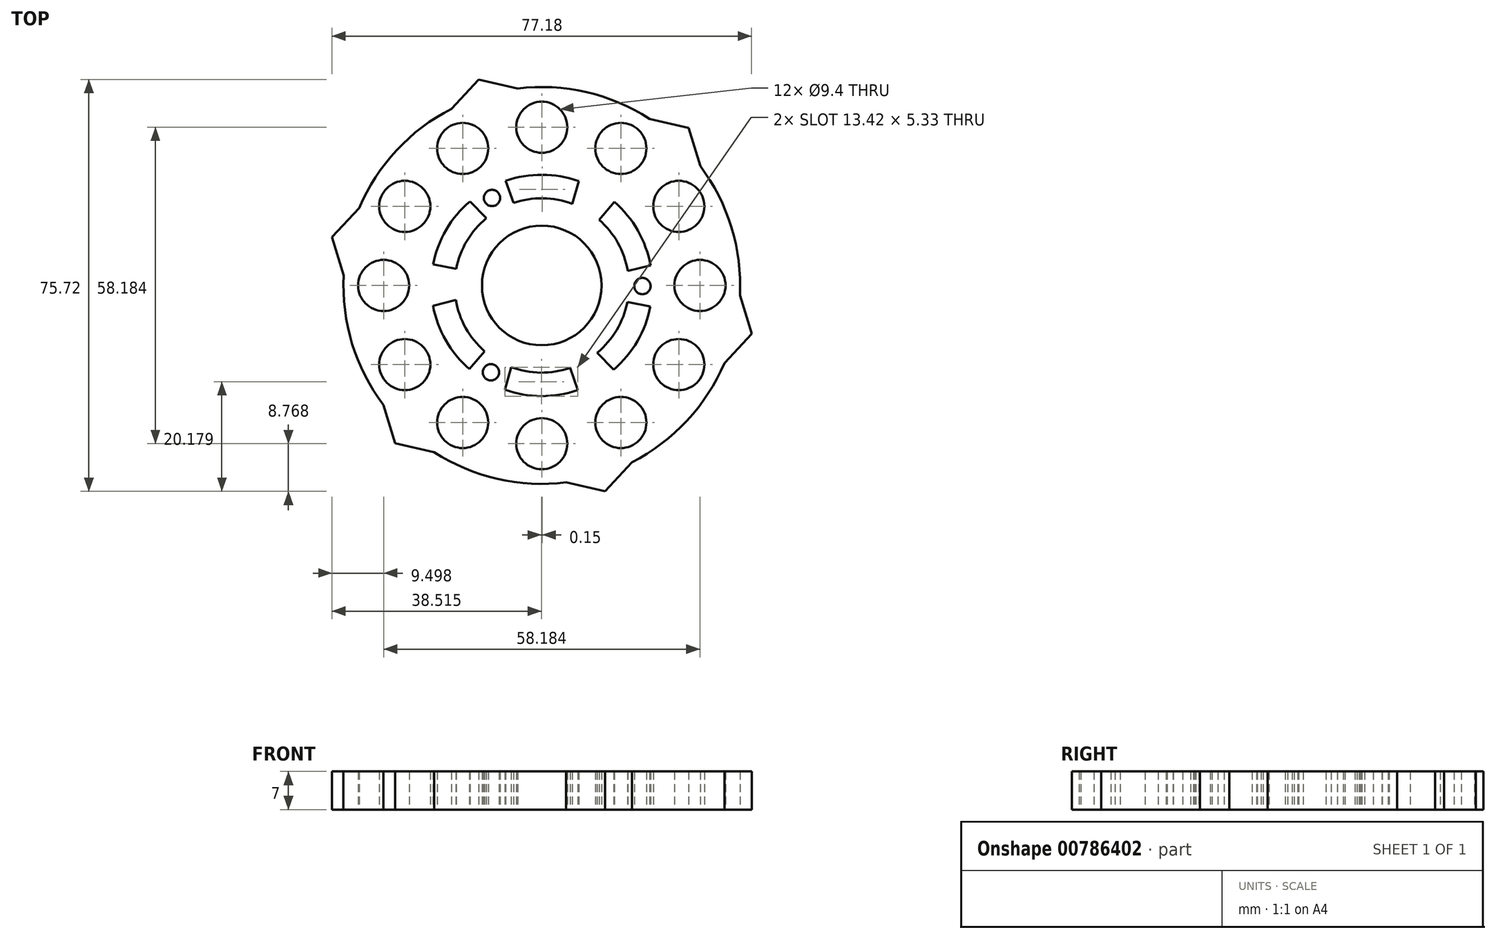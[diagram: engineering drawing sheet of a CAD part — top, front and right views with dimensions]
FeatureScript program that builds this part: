
annotation { "Feature Type Name" : "Feature", "Feature Type Description" : "" }
export const myFeature = defineFeature(function(context is Context, id is Id, definition is map)
    precondition{}
    {
        {
            var Q0;
            Q0=qCreatedBy(makeId("Top.planeOp"),FACE);
            var sketch = newSketch(context, id + "F0", { "sketchPlane" : qUnion([Q0])});
            skArc(sketch, "E0", {"start": v(-9.53, -5.5) * mm, "mid": v(0, -11) * mm, "end": v(9.53, -5.5) * mm});
            skArc(sketch, "E1", {"start": v(-19.81, -30.63) * mm, "mid": v(-8.17, -35.55) * mm, "end": v(4.44, -36.2) * mm});
            skLineSegment(sketch, "E2.2", {"start": v(11.61, -37.86) * mm, "end": v(4.44, -36.2) * mm});
            skLineSegment(sketch, "E2.3", {"start": v(-26.98, -28.98) * mm, "end": v(-29.14, -21.95) * mm});
            skLineSegment(sketch, "E2.5", {"start": v(-11.61, 37.86) * mm, "end": v(-4.44, 36.2) * mm});
            skArc(sketch, "E3.trimOffspring", {"start": v(16.62, -32.47) * mm, "mid": v(25.14, -26.44) * mm, "end": v(31.6, -18.24) * mm});
            skLineSegment(sketch, "E4.trimOffspring", {"start": v(-19.81, -30.63) * mm, "end": v(-26.98, -28.98) * mm});
            skLineSegment(sketch, "E5.trimOffspring", {"start": v(16.62, -32.47) * mm, "end": v(11.61, -37.86) * mm});
            skLineSegment(sketch, "E6.trimOffspring", {"start": v(-16.62, 32.47) * mm, "end": v(-11.61, 37.86) * mm});
            skArc(sketch, "E7.trimOffspring", {"start": v(-31.6, -18.24) * mm, "mid": v(-30.42, -20.13) * mm, "end": v(-29.14, -21.95) * mm});
            skPoint(sketch, "E8.trimOffspring.end.orphan", {"position": v(42.43, -24.5) * mm});
            skPoint(sketch, "E9.MirrorCS.end.orphan", {"position": v(-42.43, -24.5) * mm});
            skArc(sketch, "E10.1.0", {"start": v(19.81, 30.63) * mm, "mid": v(10.33, 34.99) * mm, "end": v(0, 36.48) * mm});
            skLineSegment(sketch, "E10.1.6", {"start": v(38.6, -8.87) * mm, "end": v(33.58, -14.26) * mm});
            skLineSegment(sketch, "E10.1.7", {"start": v(36.43, -1.84) * mm, "end": v(38.6, -8.87) * mm});
            skArc(sketch, "E10.1.8", {"start": v(31.6, -18.24) * mm, "mid": v(32.65, -16.28) * mm, "end": v(33.58, -14.26) * mm});
            skArc(sketch, "E10.1.9", {"start": v(36.43, -1.84) * mm, "mid": v(34.88, 10.7) * mm, "end": v(29.14, 21.95) * mm});
            skLineSegment(sketch, "E10.1.10", {"start": v(26.98, 28.98) * mm, "end": v(29.14, 21.95) * mm});
            skArc(sketch, "E10.1.11", {"start": v(9.53, -5.5) * mm, "mid": v(9.53, 5.5) * mm, "end": v(0, 11) * mm});
            skLineSegment(sketch, "E10.1.12", {"start": v(19.81, 30.63) * mm, "end": v(26.98, 28.98) * mm});
            skArc(sketch, "E10.2.0", {"start": v(-36.43, 1.84) * mm, "mid": v(-35.46, -8.55) * mm, "end": v(-31.6, -18.24) * mm});
            skArc(sketch, "E10.2.8", {"start": v(0, 36.48) * mm, "mid": v(-2.23, 36.41) * mm, "end": v(-4.44, 36.2) * mm});
            skArc(sketch, "E10.2.9", {"start": v(-16.62, 32.47) * mm, "mid": v(-26.7, 24.86) * mm, "end": v(-33.58, 14.26) * mm});
            skLineSegment(sketch, "E10.2.10", {"start": v(-38.6, 8.87) * mm, "end": v(-33.58, 14.26) * mm});
            skArc(sketch, "E10.2.11", {"start": v(0, 11) * mm, "mid": v(-9.53, 5.5) * mm, "end": v(-9.53, -5.5) * mm});
            skLineSegment(sketch, "E10.2.12", {"start": v(-36.43, 1.84) * mm, "end": v(-38.6, 8.87) * mm});
            skPoint(sketch, "E11.center.orphan", {"position": v(0, -25.62) * mm});
            skPoint(sketch, "E12.center.orphan", {"position": v(0, 29.1) * mm});
            skPoint(sketch, "E13.center.orphan", {"position": v(0, 18.27) * mm});
            skCircle(sketch, "E14", {"center": v(0, 29.1) * mm, "radius": 4.7 * mm});
            skCircle(sketch, "E15.1.0", {"center": v(-14.55, 25.2) * mm, "radius": 4.7 * mm});
            skCircle(sketch, "E15.2.0", {"center": v(-25.2, 14.55) * mm, "radius": 4.7 * mm});
            skCircle(sketch, "E15.3.0", {"center": v(-29.1, 0) * mm, "radius": 4.7 * mm});
            skCircle(sketch, "E15.4.0", {"center": v(-25.2, -14.55) * mm, "radius": 4.7 * mm});
            skCircle(sketch, "E15.5.0", {"center": v(-14.55, -25.2) * mm, "radius": 4.7 * mm});
            skCircle(sketch, "E15.6.0", {"center": v(0, -29.1) * mm, "radius": 4.7 * mm});
            skCircle(sketch, "E15.7.0", {"center": v(14.55, -25.2) * mm, "radius": 4.7 * mm});
            skCircle(sketch, "E15.8.0", {"center": v(25.2, -14.55) * mm, "radius": 4.7 * mm});
            skCircle(sketch, "E15.9.0", {"center": v(29.1, 0) * mm, "radius": 4.7 * mm});
            skCircle(sketch, "E15.10.0", {"center": v(25.2, 14.55) * mm, "radius": 4.7 * mm});
            skCircle(sketch, "E15.11.0", {"center": v(14.55, 25.2) * mm, "radius": 4.7 * mm});
            skArc(sketch, "E16", {"start": v(6.78, 19.18) * mm, "mid": v(0.08, 20.35) * mm, "end": v(-6.64, 19.23) * mm});
            skArc(sketch, "E17", {"start": v(5.6, 15.02) * mm, "mid": v(0.21, 16.03) * mm, "end": v(-5.2, 15.16) * mm});
            skLineSegment(sketch, "E18", {"start": v(-6.64, 19.23) * mm, "end": v(-5.2, 15.16) * mm});
            skLineSegment(sketch, "E19", {"start": v(6.78, 19.18) * mm, "end": v(5.6, 15.02) * mm});
            skArc(sketch, "E20.1.0", {"start": v(-10.2, 12.37) * mm, "mid": v(-13.77, 8.2) * mm, "end": v(-15.73, 3.07) * mm});
            skArc(sketch, "E20.1.1", {"start": v(-13.22, 15.47) * mm, "mid": v(-17.58, 10.24) * mm, "end": v(-19.97, 3.87) * mm});
            skLineSegment(sketch, "E20.1.2", {"start": v(-13.22, 15.47) * mm, "end": v(-10.2, 12.37) * mm});
            skLineSegment(sketch, "E20.1.3", {"start": v(-19.97, 3.87) * mm, "end": v(-15.73, 3.07) * mm});
            skArc(sketch, "E20.2.0", {"start": v(-15.8, -2.65) * mm, "mid": v(-13.99, -7.83) * mm, "end": v(-10.52, -12.1) * mm});
            skArc(sketch, "E20.2.1", {"start": v(-20, -3.71) * mm, "mid": v(-17.66, -10.1) * mm, "end": v(-13.34, -15.36) * mm});
            skLineSegment(sketch, "E20.2.2", {"start": v(-20, -3.71) * mm, "end": v(-15.8, -2.65) * mm});
            skLineSegment(sketch, "E20.2.3", {"start": v(-13.34, -15.36) * mm, "end": v(-10.52, -12.1) * mm});
            skArc(sketch, "E20.3.0", {"start": v(-5.6, -15.02) * mm, "mid": v(-0.21, -16.03) * mm, "end": v(5.2, -15.16) * mm});
            skArc(sketch, "E20.3.1", {"start": v(-6.78, -19.18) * mm, "mid": v(-0.08, -20.35) * mm, "end": v(6.64, -19.23) * mm});
            skLineSegment(sketch, "E20.3.2", {"start": v(-6.78, -19.18) * mm, "end": v(-5.6, -15.02) * mm});
            skLineSegment(sketch, "E20.3.3", {"start": v(6.64, -19.23) * mm, "end": v(5.2, -15.16) * mm});
            skArc(sketch, "E20.4.0", {"start": v(10.2, -12.37) * mm, "mid": v(13.77, -8.2) * mm, "end": v(15.73, -3.07) * mm});
            skArc(sketch, "E20.4.1", {"start": v(13.22, -15.47) * mm, "mid": v(17.58, -10.24) * mm, "end": v(19.97, -3.87) * mm});
            skLineSegment(sketch, "E20.4.2", {"start": v(13.22, -15.47) * mm, "end": v(10.2, -12.37) * mm});
            skLineSegment(sketch, "E20.4.3", {"start": v(19.97, -3.87) * mm, "end": v(15.73, -3.07) * mm});
            skArc(sketch, "E20.5.0", {"start": v(15.8, 2.65) * mm, "mid": v(13.99, 7.83) * mm, "end": v(10.52, 12.1) * mm});
            skArc(sketch, "E20.5.1", {"start": v(20, 3.71) * mm, "mid": v(17.66, 10.1) * mm, "end": v(13.34, 15.36) * mm});
            skLineSegment(sketch, "E20.5.2", {"start": v(20, 3.71) * mm, "end": v(15.8, 2.65) * mm});
            skLineSegment(sketch, "E20.5.3", {"start": v(13.34, 15.36) * mm, "end": v(10.52, 12.1) * mm});
            skCircle(sketch, "E21", {"center": v(-9.15, 16.09) * mm, "radius": 1.5 * mm});
            skCircle(sketch, "E22.1.0", {"center": v(-9.35, -15.97) * mm, "radius": 1.5 * mm});
            skCircle(sketch, "E22.2.0", {"center": v(18.5, -0.12) * mm, "radius": 1.5 * mm});
            skSolve(sketch);
        }
        {
            var Q0;
            Q0 = qSketchRegion(id + "F0", true);
            extrude(context, id + "F1", {"entities" : qUnion([Q0]), "depth" : 7 * mm, "offsetDistance" : 25 * mm});
        }
    });
